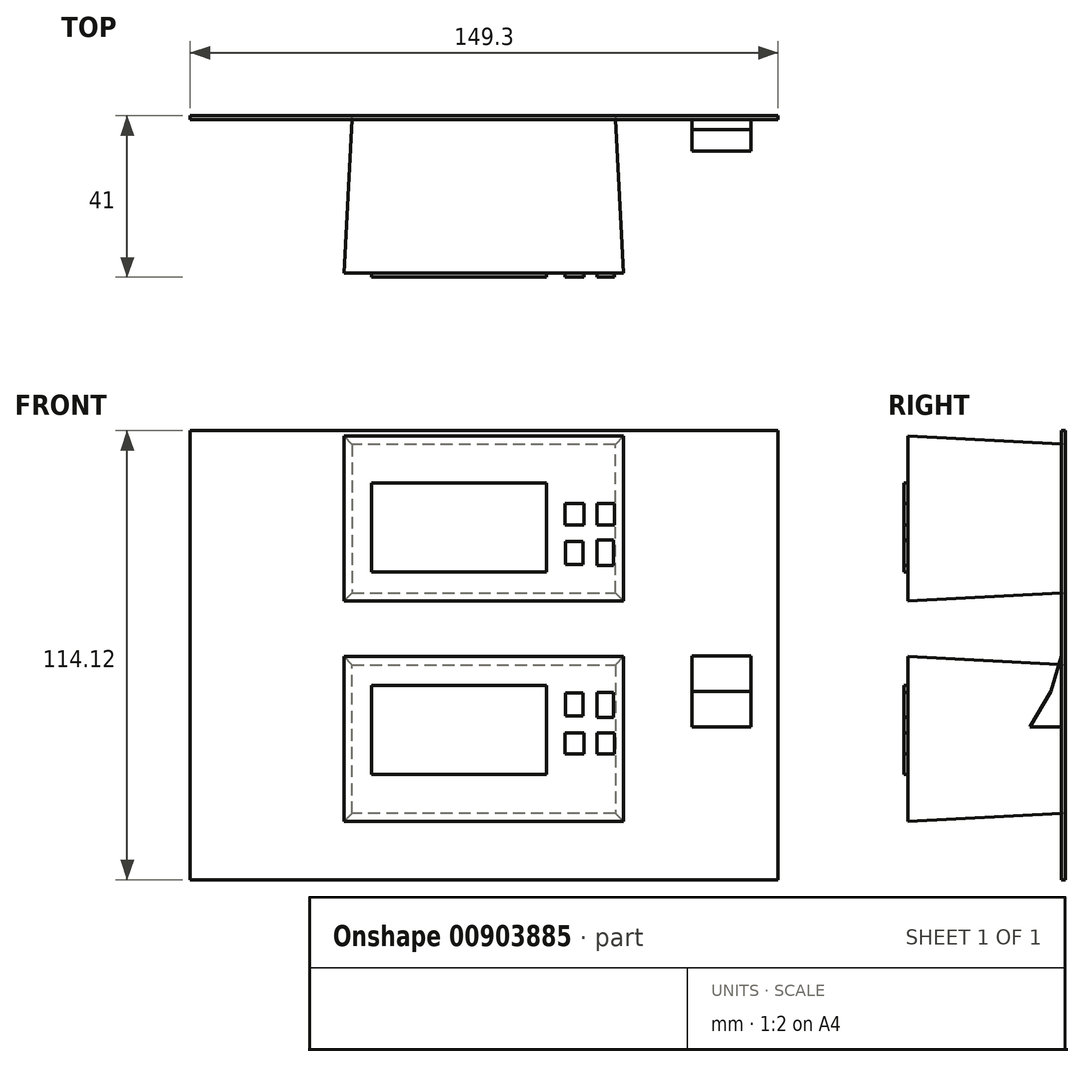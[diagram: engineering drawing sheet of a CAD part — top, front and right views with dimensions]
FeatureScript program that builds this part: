
annotation { "Feature Type Name" : "Feature", "Feature Type Description" : "" }
export const myFeature = defineFeature(function(context is Context, id is Id, definition is map)
    precondition{}
    {
        {
            var Q0;
            Q0=qCreatedBy(makeId("Front.planeOp"),FACE);
            var sketch = newSketch(context, id + "F0", { "sketchPlane" : qUnion([Q0])});
            skLineSegment(sketch, "E0.bottom", {"start": v(-33.45, 18.85) * mm, "end": v(33.45, 18.85) * mm});
            skLineSegment(sketch, "E0.top", {"start": v(-33.45, -18.85) * mm, "end": v(33.45, -18.85) * mm});
            skLineSegment(sketch, "E0.left", {"start": v(-33.45, 18.85) * mm, "end": v(-33.45, -18.85) * mm});
            skLineSegment(sketch, "E0.right", {"start": v(33.45, 18.85) * mm, "end": v(33.45, -18.85) * mm});
            skPoint(sketch, "E0.middle", {"position": v(0, 0) * mm});
            skSolve(sketch);
        }
        {
            var Q0;
            Q0 = qSketchRegion(id + "F0", true);
            extrude(context, id + "F1", {"entities" : qUnion([Q0]), "depth" : 40 * mm, "offsetDistance" : 25 * mm, "hasDraft" : true, "draftAngle" : 3 * degree});
        }
        {
            var Q0;
            Q0=makeQuery(id+"F1.opExtrude","CAP_FACE",FACE,{"disambiguationData":[OSD([sQuery(id+"F0.wireOp",EDGE,"E0.bottom"),sQuery(id+"F0.wireOp",EDGE,"E0.top"),sQuery(id+"F0.wireOp",EDGE,"E0.left"),sQuery(id+"F0.wireOp",EDGE,"E0.right")])],"isStart":false});
            var sketch = newSketch(context, id + "F2", { "sketchPlane" : qUnion([Q0])});
            skLineSegment(sketch, "E1.bottom", {"start": v(-28.48, 13.6) * mm, "end": v(15.99, 13.6) * mm});
            skLineSegment(sketch, "E1.top", {"start": v(-28.48, -9.03) * mm, "end": v(15.99, -9.03) * mm});
            skLineSegment(sketch, "E1.left", {"start": v(-28.48, 13.6) * mm, "end": v(-28.48, -9.03) * mm});
            skLineSegment(sketch, "E1.right", {"start": v(15.99, 13.6) * mm, "end": v(15.99, -9.03) * mm});
            skLineSegment(sketch, "E2.bottom", {"start": v(20.82, 11.66) * mm, "end": v(25.27, 11.66) * mm});
            skLineSegment(sketch, "E2.top", {"start": v(20.82, 5.86) * mm, "end": v(25.27, 5.86) * mm});
            skLineSegment(sketch, "E2.left", {"start": v(20.82, 11.66) * mm, "end": v(20.82, 5.86) * mm});
            skLineSegment(sketch, "E2.right", {"start": v(25.27, 11.66) * mm, "end": v(25.27, 5.86) * mm});
            skLineSegment(sketch, "E3.bottom", {"start": v(28.75, 11.85) * mm, "end": v(33, 11.85) * mm});
            skLineSegment(sketch, "E3.top", {"start": v(28.75, 5.47) * mm, "end": v(33, 5.47) * mm});
            skLineSegment(sketch, "E3.left", {"start": v(28.75, 11.85) * mm, "end": v(28.75, 5.47) * mm});
            skLineSegment(sketch, "E3.right", {"start": v(33, 11.85) * mm, "end": v(33, 5.47) * mm});
            skLineSegment(sketch, "E4.bottom", {"start": v(20.63, 1.6) * mm, "end": v(25.46, 1.6) * mm});
            skLineSegment(sketch, "E4.top", {"start": v(20.63, -3.8) * mm, "end": v(25.46, -3.8) * mm});
            skLineSegment(sketch, "E4.left", {"start": v(20.63, 1.6) * mm, "end": v(20.63, -3.8) * mm});
            skLineSegment(sketch, "E4.right", {"start": v(25.46, 1.6) * mm, "end": v(25.46, -3.8) * mm});
            skLineSegment(sketch, "E5.bottom", {"start": v(28.75, 1.6) * mm, "end": v(33.2, 1.6) * mm});
            skLineSegment(sketch, "E5.top", {"start": v(28.75, -3.8) * mm, "end": v(33.2, -3.8) * mm});
            skLineSegment(sketch, "E5.left", {"start": v(28.75, 1.6) * mm, "end": v(28.75, -3.8) * mm});
            skLineSegment(sketch, "E5.right", {"start": v(33.2, 1.6) * mm, "end": v(33.2, -3.8) * mm});
            skSolve(sketch);
        }
        {
            var Q0;
            Q0 = qSketchRegion(id + "F2", true);
            extrude(context, id + "F3", {"entities" : qUnion([Q0]), "depth" : 1 * mm, "offsetDistance" : 25 * mm});
        }
        {
            var Q0;
            Q0=qCreatedBy(makeId("Top.planeOp"),FACE);
            cPlane(context, id + "F4", {"entities" : qUnion([Q0]), "cplaneType" : CPlaneType.OFFSET, "offset" : 28 * mm, "width" : 150 * mm, "height" : 150 * mm});
        }
        {
            var Q0;
            Q0=makeQuery(id+"F1.opExtrude","SWEPT_BODY",BODY,{"disambiguationData":[OSD([sQuery(id+"F0.wireOp",EDGE,"E0.bottom"),sQuery(id+"F0.wireOp",EDGE,"E0.top"),sQuery(id+"F0.wireOp",EDGE,"E0.left"),sQuery(id+"F0.wireOp",EDGE,"E0.right")])]});
            var Q1;
            Q1=makeQuery(id+"F3.opExtrude","SWEPT_BODY",BODY,{"disambiguationData":[OSD([sQuery(id+"F2.wireOp",EDGE,"E1.bottom"),sQuery(id+"F2.wireOp",EDGE,"E1.top"),sQuery(id+"F2.wireOp",EDGE,"E1.left"),sQuery(id+"F2.wireOp",EDGE,"E1.right")])]});
            var Q2;
            Q2=makeQuery(id+"F3.opExtrude","SWEPT_BODY",BODY,{"disambiguationData":[OSD([sQuery(id+"F2.wireOp",EDGE,"E2.bottom"),sQuery(id+"F2.wireOp",EDGE,"E2.top"),sQuery(id+"F2.wireOp",EDGE,"E2.left"),sQuery(id+"F2.wireOp",EDGE,"E2.right")])]});
            var Q3;
            Q3=makeQuery(id+"F3.opExtrude","SWEPT_BODY",BODY,{"disambiguationData":[OSD([sQuery(id+"F2.wireOp",EDGE,"E3.bottom"),sQuery(id+"F2.wireOp",EDGE,"E3.top"),sQuery(id+"F2.wireOp",EDGE,"E3.left"),sQuery(id+"F2.wireOp",EDGE,"E3.right")])]});
            var Q4;
            Q4=makeQuery(id+"F3.opExtrude","SWEPT_BODY",BODY,{"disambiguationData":[OSD([sQuery(id+"F2.wireOp",EDGE,"E4.bottom"),sQuery(id+"F2.wireOp",EDGE,"E4.top"),sQuery(id+"F2.wireOp",EDGE,"E4.left"),sQuery(id+"F2.wireOp",EDGE,"E4.right")])]});
            var Q5;
            Q5=makeQuery(id+"F3.opExtrude","SWEPT_BODY",BODY,{"disambiguationData":[OSD([sQuery(id+"F2.wireOp",EDGE,"E5.bottom"),sQuery(id+"F2.wireOp",EDGE,"E5.top"),sQuery(id+"F2.wireOp",EDGE,"E5.left"),sQuery(id+"F2.wireOp",EDGE,"E5.right")])]});
            var Q6;
            Q6=qCreatedBy(id+"F4.planeOp",FACE);
            mirror(context, id + "F5", {"entities" : qUnion([Q0, Q1, Q2, Q3, Q4, Q5]), "mirrorPlane" : qUnion([Q6])});
        }
        {
            var Q0;
            Q0=qCreatedBy(makeId("Front.planeOp"),FACE);
            var sketch = newSketch(context, id + "F6", { "sketchPlane" : qUnion([Q0])});
            skLineSegment(sketch, "E6.bottom", {"start": v(74.72, 78.37) * mm, "end": v(-74.58, 78.37) * mm});
            skLineSegment(sketch, "E6.top", {"start": v(74.72, -35.75) * mm, "end": v(-74.58, -35.75) * mm});
            skLineSegment(sketch, "E6.left", {"start": v(74.72, 78.37) * mm, "end": v(74.72, -35.75) * mm});
            skLineSegment(sketch, "E6.right", {"start": v(-74.58, 78.37) * mm, "end": v(-74.58, -35.75) * mm});
            skSolve(sketch);
        }
        {
            var Q0;
            Q0 = qSketchRegion(id + "F6", true);
            extrude(context, id + "F7", {"entities" : qUnion([Q0]), "depth" : 1 * mm, "offsetDistance" : 25 * mm});
        }
        {
            var Q0;
            Q0=makeQuery(id+"F7.opExtrude","CAP_FACE",FACE,{"disambiguationData":[OSD([sQuery(id+"F6.wireOp",EDGE,"E6.bottom"),sQuery(id+"F6.wireOp",EDGE,"E6.top"),sQuery(id+"F6.wireOp",EDGE,"E6.left"),sQuery(id+"F6.wireOp",EDGE,"E6.right")])],"isStart":false});
            var sketch = newSketch(context, id + "F8", { "sketchPlane" : qUnion([Q0])});
            skLineSegment(sketch, "E7.bottom", {"start": v(52.87, 21.13) * mm, "end": v(67.9, 21.13) * mm});
            skLineSegment(sketch, "E7.top", {"start": v(52.87, 3.14) * mm, "end": v(67.9, 3.14) * mm});
            skLineSegment(sketch, "E7.left", {"start": v(52.87, 21.13) * mm, "end": v(52.87, 3.14) * mm});
            skLineSegment(sketch, "E7.right", {"start": v(67.9, 21.13) * mm, "end": v(67.9, 3.14) * mm});
            skSolve(sketch);
        }
        {
            var Q0;
            Q0 = qSketchRegion(id + "F8", true);
            extrude(context, id + "F9", {"entities" : qUnion([Q0]), "operationType" : NewBodyOperationType.ADD, "depth" : 8 * mm, "offsetDistance" : 25 * mm});
        }
        {
            var Q0;
            Q0=makeQuery(id+"F9.opExtrude","SWEPT_FACE",FACE,{"disambiguationData":[OSD([sQuery(id+"F8.wireOp",EDGE,"E7.right")])]});
            var sketch = newSketch(context, id + "F10", { "sketchPlane" : qUnion([Q0])});
            skLineSegment(sketch, "E8", {"start": v(-1, 21.13) * mm, "end": v(-3.58, 12.14) * mm});
            skPoint(sketch, "E8.endSnap0", {"position": v(-9, 12.14) * mm});
            skLineSegment(sketch, "E9", {"start": v(-3.58, 12.14) * mm, "end": v(-9, 3.14) * mm});
            skLineSegment(sketch, "E10", {"start": v(-9, 3.14) * mm, "end": v(-9, 21.13) * mm});
            skLineSegment(sketch, "E11", {"start": v(-9, 21.13) * mm, "end": v(-1, 21.13) * mm});
            skSolve(sketch);
        }
        {
            var Q0;
            Q0 = qSketchRegion(id + "F10", true);
            extrude(context, id + "F11", {"entities" : qUnion([Q0]), "operationType" : NewBodyOperationType.REMOVE, "oppositeDirection" : true, "depth" : 16.9 * mm, "offsetDistance" : 25 * mm});
        }
    });
